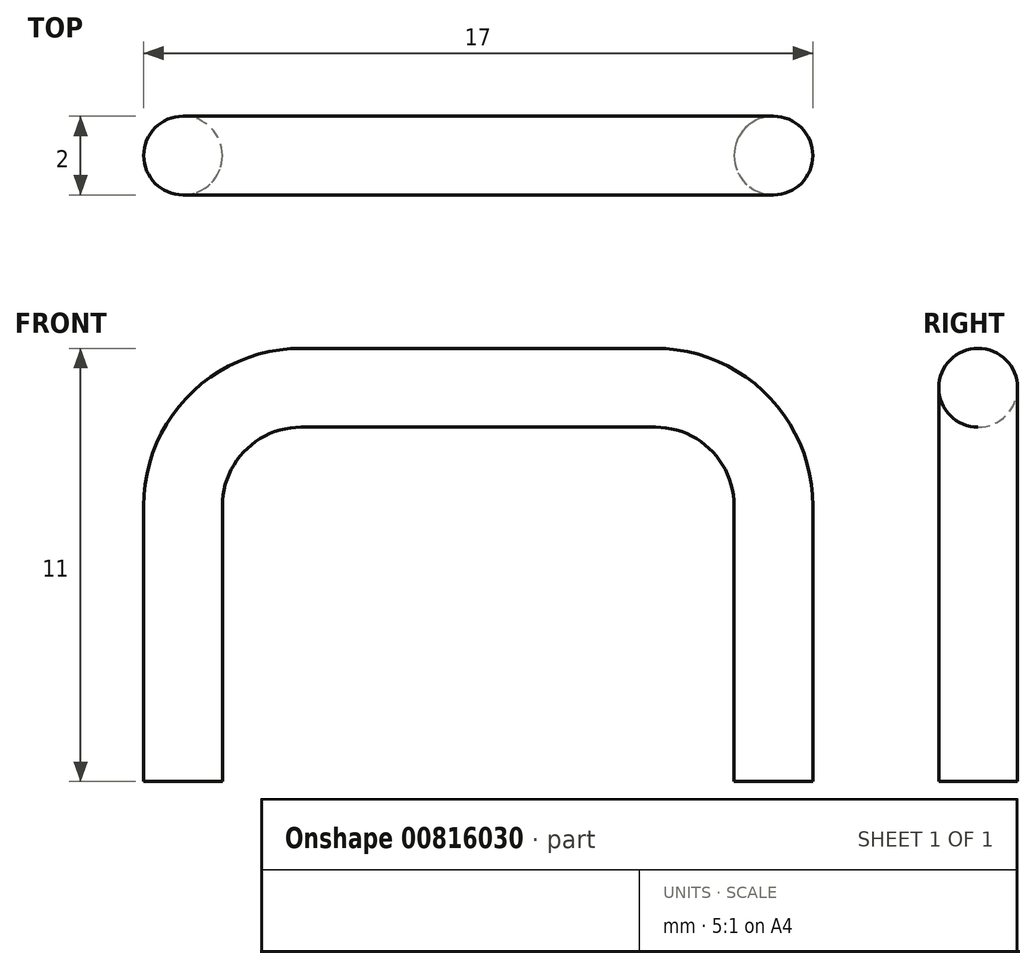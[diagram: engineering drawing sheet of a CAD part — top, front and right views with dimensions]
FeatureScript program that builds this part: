
annotation { "Feature Type Name" : "Feature", "Feature Type Description" : "" }
export const myFeature = defineFeature(function(context is Context, id is Id, definition is map)
    precondition{}
    {
        {
            var Q0;
            Q0=qCreatedBy(makeId("Front.planeOp"),FACE);
            var sketch = newSketch(context, id + "F0", { "sketchPlane" : qUnion([Q0])});
            skLineSegment(sketch, "E0", {"start": v(0, 0) * mm, "end": v(0, 7) * mm});
            skLineSegment(sketch, "E1", {"start": v(3, 10) * mm, "end": v(12, 10) * mm});
            skLineSegment(sketch, "E2", {"start": v(15, 7) * mm, "end": v(15, 0) * mm});
            skPoint(sketch, "E3.visualSharp", {"position": v(0, 10) * mm});
            skArc(sketch, "E3.filletArc", {"start": v(3, 10) * mm, "mid": v(0.88, 9.12) * mm, "end": v(0, 7) * mm});
            skPoint(sketch, "E4.visualSharp", {"position": v(15, 10) * mm});
            skArc(sketch, "E4.filletArc", {"start": v(15, 7) * mm, "mid": v(14.12, 9.12) * mm, "end": v(12, 10) * mm});
            skSolve(sketch);
        }
        {
            var Q0;
            Q0=qCreatedBy(makeId("Top.planeOp"),FACE);
            var sketch = newSketch(context, id + "F1", { "sketchPlane" : qUnion([Q0])});
            skCircle(sketch, "E5", {"center": v(0, 0) * mm, "radius": 1 * mm});
            skSolve(sketch);
        }
        {
            var Q0;
            Q0=makeQuery(id+"F1.imprint","IMPRINT",FACE,{"disambiguationData":[TD([[makeQuery(id+"F1.imprint","IMPRINT",EDGE,{"derivedFrom":sQuery(id+"F1.wireOp",EDGE,"E5")}),1.0]])]});
            var Q1;
            Q1=sQuery(id+"F0.wireOp",EDGE,"E0");
            var Q2;
            Q2=sQuery(id+"F0.wireOp",EDGE,"E3.filletArc");
            var Q3;
            Q3=sQuery(id+"F0.wireOp",EDGE,"E1");
            var Q4;
            Q4=sQuery(id+"F0.wireOp",EDGE,"E4.filletArc");
            var Q5;
            Q5=sQuery(id+"F0.wireOp",EDGE,"E2");
            sweep(context, id + "F2", {"profiles" : qUnion([Q0]), "path" : qUnion([Q1, Q2, Q3, Q4, Q5])});
        }
    });
